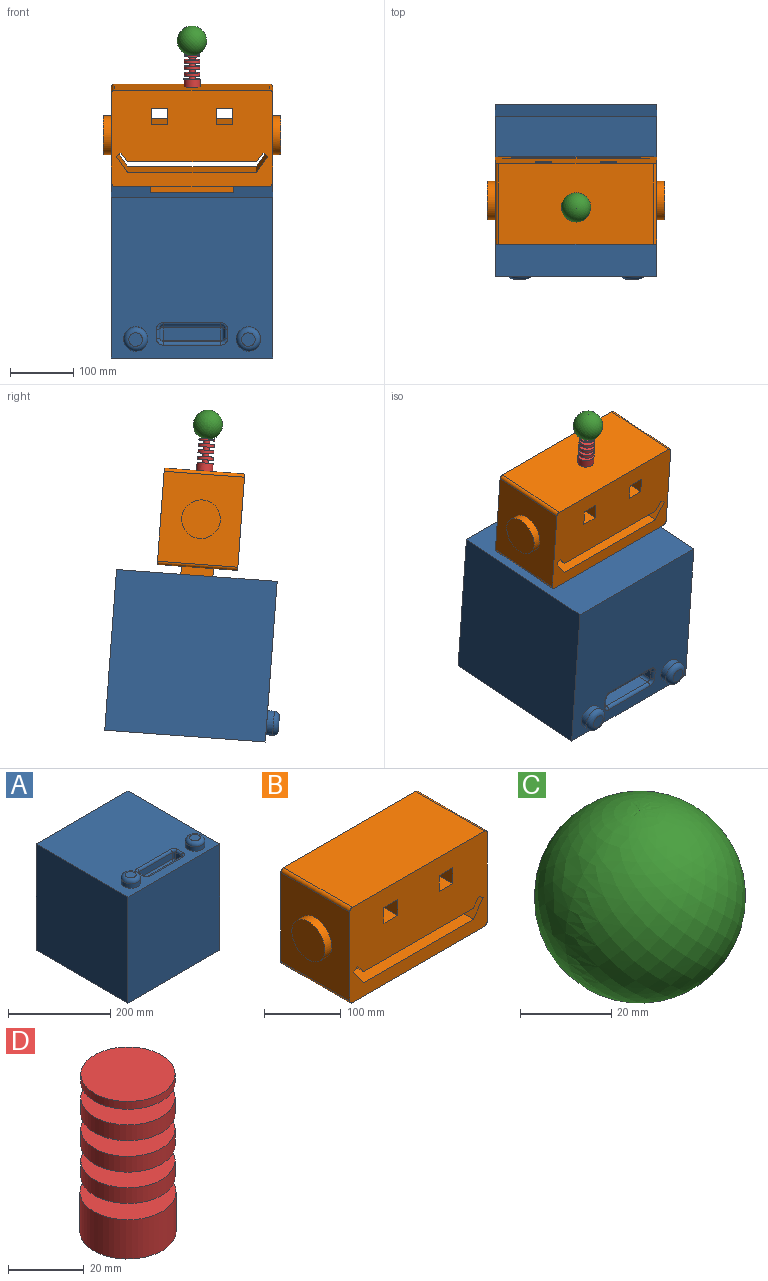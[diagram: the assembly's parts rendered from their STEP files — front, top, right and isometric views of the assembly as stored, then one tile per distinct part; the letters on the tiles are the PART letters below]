
ASSEMBLY  parts=4 mates=3
PART A: 34 faces, bbox 254x254x273.1 mm
  f0: plane 254x254mm, normal (0,0,1), area 58350.2mm2, adj f1,f2,f3,f4,f12,f14,f15,f19
  f1: plane 254x254mm, normal (1,0,0), area 64516mm2, adj f0,f2,f4,f5
  f2: plane 254x254mm, normal (0,1,0), area 64516mm2, adj f0,f1,f3,f5
  f3: plane 254x254mm, normal (-1,0,0), area 64516mm2, adj f0,f2,f4,f5
  f4: plane 254x254mm, normal (0,-1,0), area 64516mm2, adj f0,f1,f3,f5
  f5: plane 254x254mm, normal (0,0,-1), area 64516mm2, adj f1,f2,f3,f4
  f6: plane 91.44x15.24mm, normal (0,-1,0), area 1393.5mm2, adj f16,f21,f24,f27
  f7: plane 15.24x15.24mm, normal (1,0,0), area 232.3mm2, adj f18,f22,f23,f27
  f8: plane 91.44x20.32mm, normal (0,1,0), area 1858.1mm2, adj f10,f11,f14,f18
  f9: plane 15.24x15.24mm, normal (-1,0,0), area 232.3mm2, adj f11,f13,f15,f16
  f10: plane 91.44x20.32mm, normal (0,0,1), area 1858.1mm2, adj f8,f13,f21,f22
  f11: cylinder r=5.08mm len=20.32mm, axis (0,0,1), area 147.4mm2, adj f8,f9,f12,f13
  f12: torus R=10.16mm, axis (0,0,1), area 86.8mm2, adj f0,f11,f14,f15
  f13: cylinder r=5.08mm len=20.32mm, axis (0,1,0), area 147.4mm2, adj f9,f10,f11,f17
  f14: cylinder r=5.08mm len=91.44mm, axis (-1,0,0), area 729.7mm2, adj f0,f8,f12,f19
  f15: cylinder r=5.08mm len=15.24mm, axis (0,-1,0), area 121.6mm2, adj f0,f9,f12,f20
  f16: cylinder r=5.08mm len=15.24mm, axis (0,0,-1), area 121.6mm2, adj f6,f9,f17,f20
  f17: sphere r=5.08mm, area 40.5mm2, adj f13,f16,f21
  f18: cylinder r=5.08mm len=20.32mm, axis (0,0,-1), area 147.4mm2, adj f7,f8,f19,f22
  f19: torus R=10.16mm, axis (0,0,1), area 86.8mm2, adj f0,f14,f18,f23
  f20: torus R=10.16mm, axis (0,0,1), area 86.8mm2, adj f0,f15,f16,f24
  f21: cylinder r=5.08mm len=91.44mm, axis (-1,0,0), area 729.7mm2, adj f6,f10,f17,f25
  f22: cylinder r=5.08mm len=20.32mm, axis (0,-1,0), area 147.4mm2, adj f7,f10,f18,f25
  f23: cylinder r=5.08mm len=15.24mm, axis (0,1,0), area 121.6mm2, adj f0,f7,f19,f26
  f24: cylinder r=5.08mm len=91.44mm, axis (1,0,0), area 729.7mm2, adj f0,f6,f20,f26
  f25: sphere r=5.08mm, area 40.5mm2, adj f21,f22,f27
  f26: torus R=10.16mm, axis (0,0,1), area 86.8mm2, adj f0,f23,f24,f27
  f27: cylinder r=5.08mm len=15.24mm, axis (0,0,1), area 121.6mm2, adj f6,f7,f25,f26
  f28: cylinder r=19.05mm len=38.1mm, axis (0,0,-1), area 1276.9mm2, adj f0,f33
  f29: plane 21.34x21.34mm, normal (0,0,1), area 357.5mm2, adj f33
  f30: cylinder r=19.05mm len=38.1mm, axis (0,0,-1), area 1276.9mm2, adj f0,f32
  f31: plane 21.34x21.34mm, normal (0,0,1), area 357.5mm2, adj f32
  f32: torus R=10.67mm, axis (0,0,1), area 1324mm2, adj f30,f31
  f33: torus R=10.67mm, axis (0,0,1), area 1324mm2, adj f28,f29
PART B: 35 faces, bbox 279.4x127x165.1 mm
  f0: plane 127x25.4mm, normal (1,0,0), area 3225.8mm2, adj f1,f19,f20,f21
  f1: plane 127x25.4mm, normal (0,0,-1), area 3225.8mm2, adj f0,f2,f20,f21
  f2: plane 127x25.4mm, normal (-1,0,0), area 3225.8mm2, adj f1,f19,f20,f21
  f3: plane 203.2x127mm, normal (0,0,1), area 25806.4mm2, adj f4,f16,f20,f21
  f4: plane 127x26.09mm, normal (0.83,0,0.56), area 4011.5mm2, adj f3,f5,f20,f21
  f5: plane 127x7.46mm, normal (0.56,0,-0.83), area 1146.9mm2, adj f4,f6,f20,f21
  f6: plane 127x13.4mm, normal (-0.79,0,-0.61), area 2149.8mm2, adj f5,f7,f20,f21
  f7: plane 203.2x127mm, normal (0,0,-1), area 25806.4mm2, adj f6,f8,f20,f21
  f8: plane 127x13.4mm, normal (0.79,0,-0.61), area 2149.8mm2, adj f7,f9,f20,f21
  f9: plane 127x7.46mm, normal (-0.56,0,-0.83), area 1146.9mm2, adj f8,f16,f20,f21
  f10: plane 127x25.4mm, normal (1,0,0), area 3225.8mm2, adj f11,f17,f20,f21
  f11: plane 127x25.4mm, normal (0,0,-1), area 3225.8mm2, adj f10,f12,f20,f21
  f12: plane 127x25.4mm, normal (-1,0,0), area 3225.8mm2, adj f11,f17,f20,f21
  f13: plane 142.24x127mm, normal (-1,0,0), area 15145.8mm2, adj f20,f21,f22,f25,f33
  f14: plane 243.84x127mm, normal (0,0,-1), area 24258mm2, adj f20,f21,f22,f23,f26,f27,f28,f29
  f15: plane 142.24x127mm, normal (1,0,0), area 15145.8mm2, adj f20,f21,f23,f24,f31
  f16: plane 127x26.09mm, normal (-0.83,0,0.56), area 4011.5mm2, adj f3,f9,f20,f21
  f17: plane 127x25.4mm, normal (0,0,1), area 3225.8mm2, adj f10,f12,f20,f21
  f18: plane 243.84x127mm, normal (0,0,1), area 30967.7mm2, adj f20,f21,f24,f25
  f19: plane 127x25.4mm, normal (0,0,1), area 3225.8mm2, adj f0,f2,f20,f21
  f20: plane 254x152.4mm, normal (0,-1,0), area 33315.1mm2, adj f0,f1,f2,f3,f4,f5,f6,f7
  f21: plane 254x152.4mm, normal (0,1,0), area 33315.1mm2, adj f0,f1,f2,f3,f4,f5,f6,f7
  f22: cylinder r=5.08mm len=127mm, axis (0,-1,0), area 1013.4mm2, adj f13,f14,f20,f21
  f23: cylinder r=5.08mm len=127mm, axis (0,1,0), area 1013.4mm2, adj f14,f15,f20,f21
  f24: cylinder r=5.08mm len=127mm, axis (0,-1,0), area 1013.4mm2, adj f15,f18,f20,f21
  f25: cylinder r=5.08mm len=127mm, axis (0,1,0), area 1013.4mm2, adj f13,f18,f20,f21
  f26: plane 132.08x12.7mm, normal (0,-1,0), area 1677.4mm2, adj f14,f27,f29,f30
  f27: plane 50.8x12.7mm, normal (-1,0,0), area 645.2mm2, adj f14,f26,f28,f30
  f28: plane 132.08x12.7mm, normal (0,1,0), area 1677.4mm2, adj f14,f27,f29,f30
  f29: plane 50.8x12.7mm, normal (1,0,0), area 645.2mm2, adj f14,f26,f28,f30
  f30: plane 132.08x50.8mm, normal (0,0,-1), area 6709.7mm2, adj f26,f27,f28,f29
  f31: cylinder r=30.48mm len=60.96mm, axis (-1,0,0), area 2432.2mm2, adj f15,f32
  f32: plane 60.96x60.96mm, normal (1,0,0), area 2918.6mm2, adj f31
  f33: cylinder r=30.48mm len=60.96mm, axis (1,0,0), area 2432.2mm2, adj f13,f34
  f34: plane 60.96x60.96mm, normal (-1,0,0), area 2918.6mm2, adj f33
PART C: 2 faces, bbox 46.4x46.4x45.7 mm
  f0: plane 13x13mm, normal (0,0,-1), area 132.8mm2, adj f1
  f1: revolved ~46.38x46.38mm, area 6647.4mm2, adj f0
PART D: 19 faces, bbox 25.4x25.4x50.8 mm
  f0: cylinder r=12.45mm len=24.9mm, axis (0,0,-1), area 198.7mm2, adj f1,f18
  f1: plane 24.9x24.9mm, normal (0,0,1), area 487mm2, adj f0
  f2: plane 25.4x25.4mm, normal (0,0,-1), area 506.7mm2, adj f3
  f3: cylinder r=12.7mm len=25.4mm, axis (0,0,-1), area 1013.4mm2, adj f2,f4
  f4: plane 25.4x25.4mm, normal (0,0,1), area 433.9mm2, adj f3,f5
  f5: cylinder r=4.82mm len=9.63mm, axis (0,0,-1), area 153.7mm2, adj f4,f6
  f6: plane 24.9x24.9mm, normal (0,0,-1), area 414.2mm2, adj f5,f7
  f7: cylinder r=12.45mm len=24.9mm, axis (0,0,-1), area 397.4mm2, adj f6,f8
  f8: plane 24.9x24.9mm, normal (0,0,1), area 414.2mm2, adj f7,f9
  f9: cylinder r=4.82mm len=9.63mm, axis (0,0,-1), area 153.7mm2, adj f8,f10
  f10: plane 24.9x24.9mm, normal (0,0,-1), area 414.2mm2, adj f9,f11
  f11: cylinder r=12.45mm len=24.9mm, axis (0,0,-1), area 397.4mm2, adj f10,f12
  f12: plane 24.9x24.9mm, normal (0,0,1), area 414.2mm2, adj f11,f13
  f13: cylinder r=4.82mm len=9.63mm, axis (0,0,-1), area 153.7mm2, adj f12,f14
  f14: plane 24.9x24.9mm, normal (0,0,-1), area 414.2mm2, adj f13,f15
  f15: cylinder r=12.45mm len=24.9mm, axis (0,0,-1), area 397.4mm2, adj f14,f16
  f16: plane 24.9x24.9mm, normal (0,0,1), area 414.2mm2, adj f15,f17
  f17: cylinder r=4.82mm len=9.63mm, axis (0,0,-1), area 153.7mm2, adj f16,f18
  f18: plane 24.9x24.9mm, normal (0,0,-1), area 414.2mm2, adj f0,f17
PLACE A rot(axis=(1,0,0),94.2deg) t=(-493.3,-49.04,-450.97)mm
PLACE B rot(axis=(1,0,0),4.2deg) t=(-493.3,-122.62,-316.31)mm
PLACE C rot(axis=(1,0,0),4.2deg) t=(-493.3,-135.28,-317.24)mm
PLACE D rot(axis=(0,-0.04,1),180deg) t=(-493.3,-236.61,-324.7)mm
MATE fastened C.f0 <-> D.f0  axis (0,0.07,-1) through (-493.3,-200.86,-118.32)mm
MATE fastened D.f0 <-> B.f18  axis (0,0.07,-1) through (-493.3,-197.13,-168.98)mm
MATE fastened B.f30 <-> A.f2  axis (0,0.07,-1) through (-493.3,-185.02,-333.64)mm
